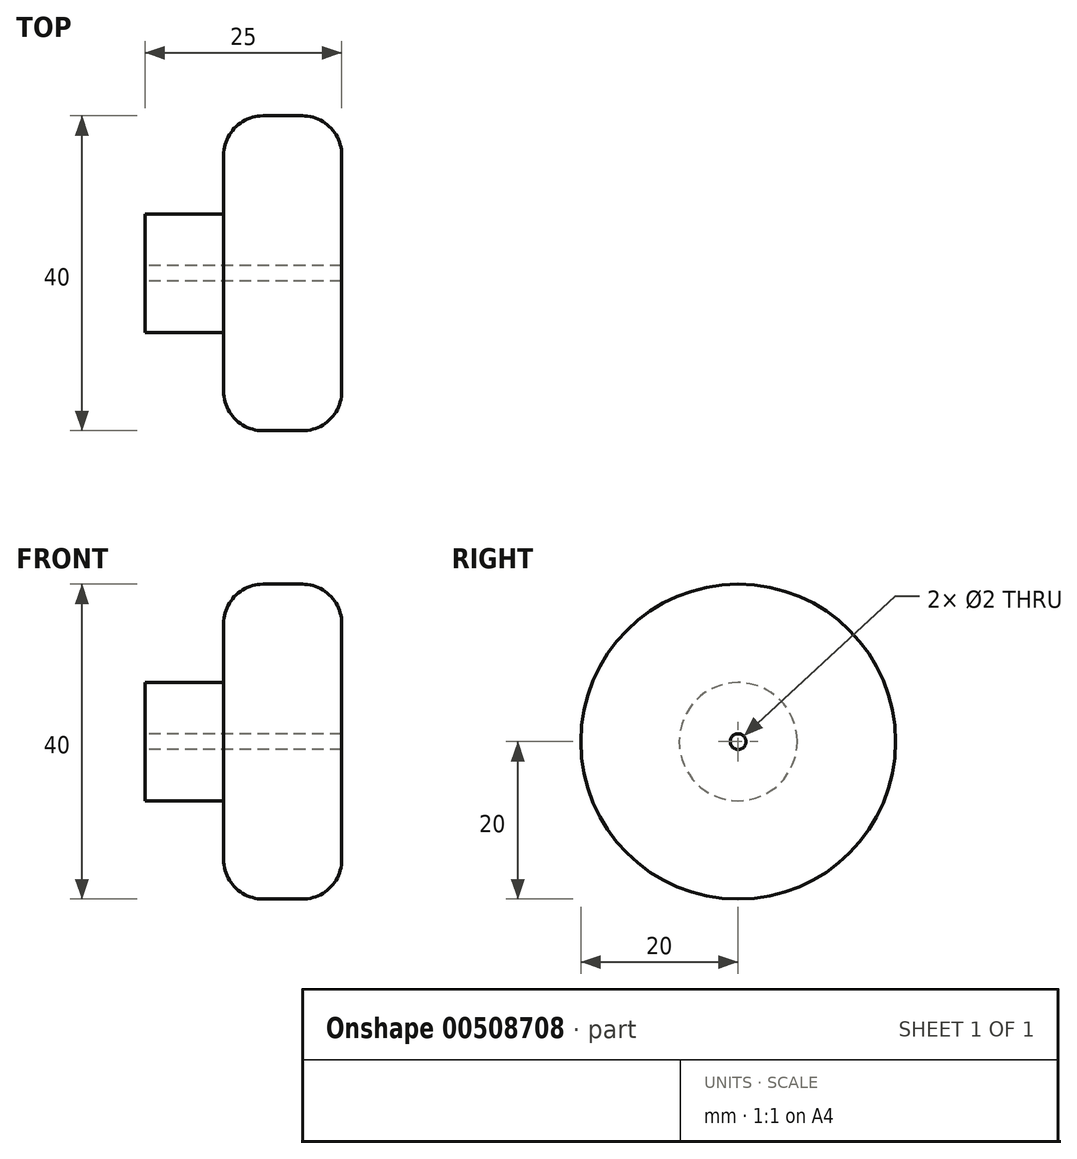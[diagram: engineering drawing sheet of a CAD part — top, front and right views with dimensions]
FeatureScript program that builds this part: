
annotation { "Feature Type Name" : "Feature", "Feature Type Description" : "" }
export const myFeature = defineFeature(function(context is Context, id is Id, definition is map)
    precondition{}
    {
        {
            var Q0;
            Q0=qCreatedBy(makeId("Front.planeOp"),FACE);
            var sketch = newSketch(context, id + "F0", { "sketchPlane" : qUnion([Q0])});
            skLineSegment(sketch, "E0.bottom", {"start": v(0, 7.5) * mm, "end": v(10, 7.5) * mm});
            skLineSegment(sketch, "E0.top", {"start": v(0, 1) * mm, "end": v(25, 1) * mm});
            skLineSegment(sketch, "E0.left", {"start": v(0, 7.5) * mm, "end": v(0, 1) * mm});
            skLineSegment(sketch, "E0.right", {"start": v(25, 7.5) * mm, "end": v(25, 1) * mm});
            skLineSegment(sketch, "E1.left", {"start": v(25, 7.5) * mm, "end": v(25, 20) * mm});
            skLineSegment(sketch, "E1.right", {"start": v(10, 7.5) * mm, "end": v(10, 20) * mm});
            skLineSegment(sketch, "E2", {"start": v(10, 20) * mm, "end": v(25, 20) * mm});
            skLineSegment(sketch, "E3", {"start": v(0, 66.32) * mm, "end": v(0, -57.72) * mm});
            skLineSegment(sketch, "E4", {"start": v(-60.71, 0) * mm, "end": v(74.91, 0) * mm, "construction": true});
            skSolve(sketch);
        }
        {
            var Q0;
            Q0=qSketchRegion(id+"F0",true);
            var Q1;
            Q1=sQuery(id+"F0.wireOp",EDGE,"E4");
            revolve(context, id + "F1", {"entities" : qUnion([Q0]), "axis" : qUnion([Q1]), "revolveType" : RevolveType.FULL});
        }
        {
            var Q0;
            Q0=makeQuery(id+"F1.opRevolve","SWEPT_EDGE",EDGE,{"disambiguationData":[OSD([sQuery(id+"F0.wireOp",EDGE,"E1.right"),sQuery(id+"F0.wireOp",EDGE,"E2")])]});
            var Q1;
            Q1=makeQuery(id+"F1.opRevolve","SWEPT_EDGE",EDGE,{"disambiguationData":[OSD([sQuery(id+"F0.wireOp",EDGE,"E1.left"),sQuery(id+"F0.wireOp",EDGE,"E2")])]});
            var Q2;
            Q2=makeQuery(id+"F1.opRevolve","SWEPT_FACE",FACE,{"disambiguationData":[OSD([sQuery(id+"F0.wireOp",EDGE,"E2")])]});
            fillet(context, id + "F2", {"entities" : qUnion([Q0, Q1, Q2]), "radius" : 5 * mm, "tangentPropagation" : true, "allowEdgeOverflow" : false});
        }
        {
            var Q0;
            Q0=qCreatedBy(makeId("Front.planeOp"),FACE);
            var Q1;
            Q1 = qBodyType(qCreatedBy(id + "F4" ,EDGE), BodyType.WIRE);
            cPlane(context, id + "F3", {"entities" : qUnion([Q0, Q1]), "cplaneType" : CPlaneType.OFFSET, "offset" : 40 * mm, "width" : 150 * mm, "height" : 150 * mm});
        }
    });
